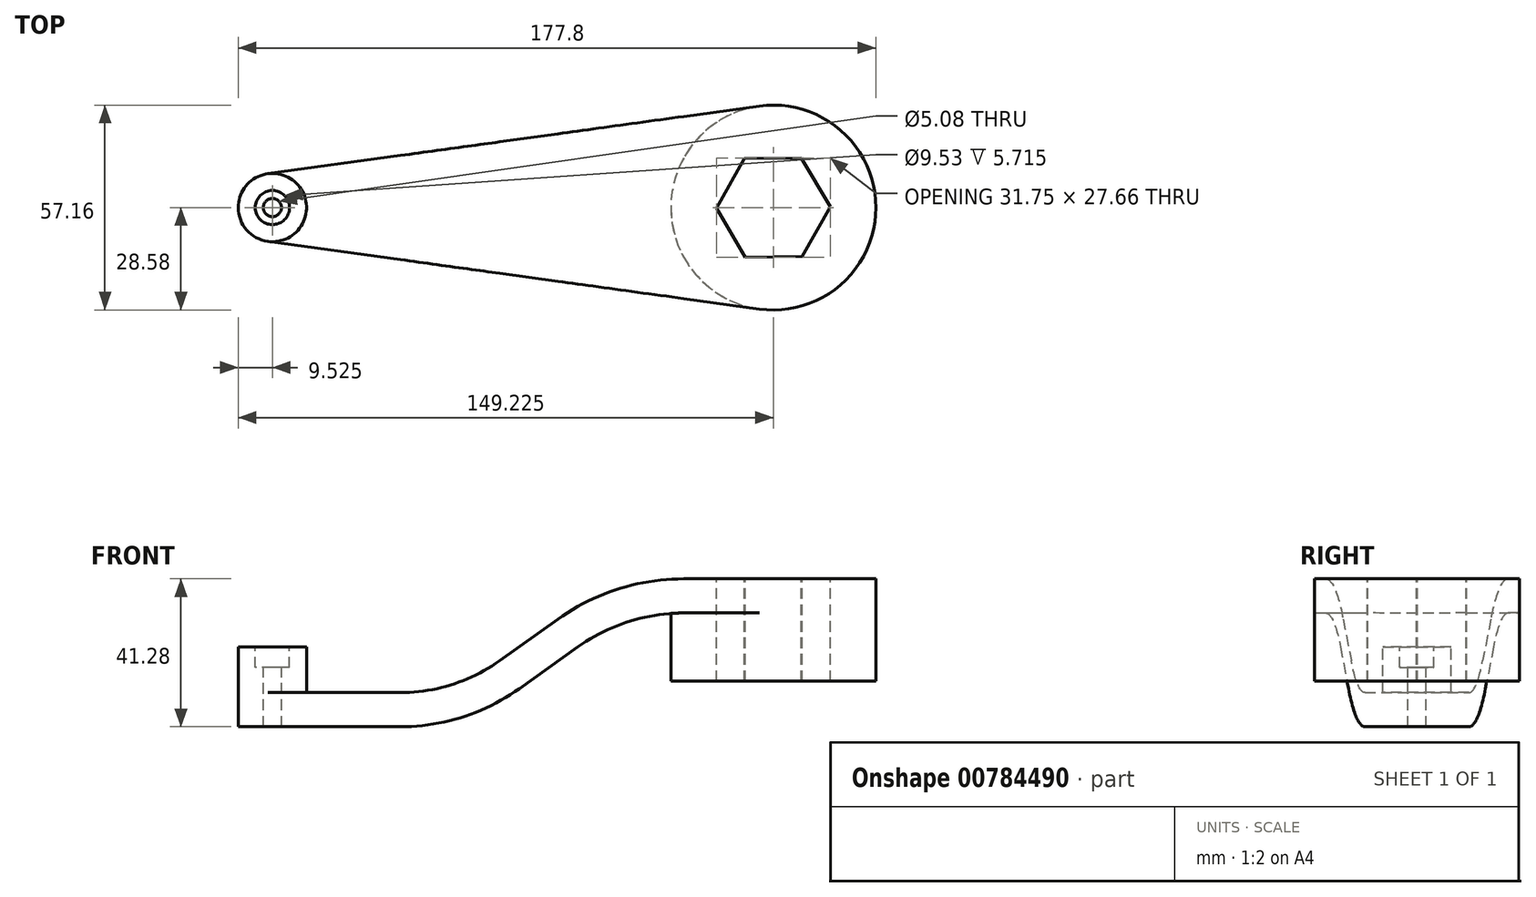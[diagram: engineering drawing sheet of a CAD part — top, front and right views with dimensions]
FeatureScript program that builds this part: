
annotation { "Feature Type Name" : "Feature", "Feature Type Description" : "" }
export const myFeature = defineFeature(function(context is Context, id is Id, definition is map)
    precondition{}
    {
        {
            var Q0;
            Q0=qCreatedBy(makeId("Front.planeOp"),FACE);
            var sketch = newSketch(context, id + "F0", { "sketchPlane" : qUnion([Q0])});
            skLineSegment(sketch, "E0", {"start": v(0, 0) * mm, "end": v(0, -9.53) * mm});
            skLineSegment(sketch, "E1", {"start": v(0, -9.53) * mm, "end": v(-53.57, -9.53) * mm});
            skPoint(sketch, "E2", {"position": v(-69.85, -9.53) * mm});
            skPoint(sketch, "E3", {"position": v(-114.3, -41.28) * mm});
            skLineSegment(sketch, "E4", {"start": v(-83.1, -18.99) * mm, "end": v(-99.4, -30.63) * mm});
            skLineSegment(sketch, "E5", {"start": v(-132.61, -41.28) * mm, "end": v(-177.8, -41.28) * mm});
            skArc(sketch, "E6.filletArc", {"start": v(-53.57, -9.52) * mm, "mid": v(-69.07, -11.95) * mm, "end": v(-83.1, -18.99) * mm});
            skArc(sketch, "E7.filletArc", {"start": v(-132.61, -41.28) * mm, "mid": v(-115.17, -38.55) * mm, "end": v(-99.4, -30.63) * mm});
            skLineSegment(sketch, "E8.0", {"start": v(-132.61, -31.75) * mm, "end": v(-177.8, -31.75) * mm});
            skArc(sketch, "E9.0", {"start": v(-132.61, -31.75) * mm, "mid": v(-118.08, -29.48) * mm, "end": v(-104.93, -22.88) * mm});
            skLineSegment(sketch, "E10.0", {"start": v(-88.63, -11.24) * mm, "end": v(-104.93, -22.88) * mm});
            skArc(sketch, "E11.0", {"start": v(-53.57, 0) * mm, "mid": v(-71.98, -2.88) * mm, "end": v(-88.63, -11.24) * mm});
            skLineSegment(sketch, "E12.0", {"start": v(0, 0) * mm, "end": v(-53.57, 0) * mm});
            skLineSegment(sketch, "E13", {"start": v(-177.8, -31.75) * mm, "end": v(-177.8, -41.28) * mm});
            skSolve(sketch);
        }
        {
            var Q0;
            Q0 = qSketchRegion(id + "F0", true);
            extrude(context, id + "F1", {"entities" : qUnion([Q0]), "endBound" : BoundingType.SYMMETRIC, "depth" : 57.15 * mm, "offsetDistance" : 25.4 * mm});
        }
        {
            var Q0;
            Q0=makeQuery(id+"F1.opExtrude","SWEPT_FACE",FACE,{"disambiguationData":[OSD([sQuery(id+"F0.wireOp",EDGE,"E12.0")])]});
            var sketch = newSketch(context, id + "F2", { "sketchPlane" : qUnion([Q0])});
            skLineSegment(sketch, "E14", {"start": v(0, 0) * mm, "end": v(-190.14, 0) * mm, "construction": true});
            skArc(sketch, "E15", {"start": v(-32.47, -28.3) * mm, "mid": v(0, 0) * mm, "end": v(-32.47, 28.3) * mm});
            skArc(sketch, "E16", {"start": v(-169.57, 9.44) * mm, "mid": v(-177.8, 0) * mm, "end": v(-169.57, -9.44) * mm});
            skLineSegment(sketch, "E17", {"start": v(-169.57, 9.44) * mm, "end": v(-32.47, 28.3) * mm});
            skLineSegment(sketch, "E18.MirrorCS", {"start": v(-169.57, -9.44) * mm, "end": v(-32.47, -28.3) * mm});
            skSolve(sketch);
        }
        {
            var Q0;
            Q0 = qSketchRegion(id + "F2", true);
            extrude(context, id + "F3", {"entities" : qUnion([Q0]), "operationType" : NewBodyOperationType.INTERSECT, "endBound" : BoundingType.THROUGH_ALL, "oppositeDirection" : true, "depth" : 25.4 * mm, "offsetDistance" : 25.4 * mm});
        }
        {
            var Q0;
            Q0=makeQuery(id+"F1.opExtrude","SWEPT_FACE",FACE,{"disambiguationData":[OSD([sQuery(id+"F0.wireOp",EDGE,"E8.0")])]});
            var sketch = newSketch(context, id + "F4", { "sketchPlane" : qUnion([Q0])});
            skCircle(sketch, "E19", {"center": v(-168.28, 0) * mm, "radius": 9.53 * mm});
            skSolve(sketch);
        }
        {
            var Q0;
            Q0 = qSketchRegion(id + "F4", true);
            extrude(context, id + "F5", {"entities" : qUnion([Q0]), "operationType" : NewBodyOperationType.ADD, "depth" : 12.7 * mm, "offsetDistance" : 25.4 * mm});
        }
        {
            var Q0;
            Q0=makeQuery(id+"F1.opExtrude","SWEPT_FACE",FACE,{"disambiguationData":[OSD([sQuery(id+"F0.wireOp",EDGE,"E1")])]});
            var sketch = newSketch(context, id + "F6", { "sketchPlane" : qUnion([Q0])});
            skCircle(sketch, "E20", {"center": v(-28.57, 0) * mm, "radius": 28.58 * mm});
            skSolve(sketch);
        }
        {
            var Q0;
            Q0 = qSketchRegion(id + "F6", true);
            extrude(context, id + "F7", {"entities" : qUnion([Q0]), "operationType" : NewBodyOperationType.ADD, "depth" : 19.05 * mm, "offsetDistance" : 25.4 * mm});
        }
        {
            var Q0;
            Q0=makeQuery(id+"F1.opExtrude","SWEPT_FACE",FACE,{"disambiguationData":[OSD([sQuery(id+"F0.wireOp",EDGE,"E12.0")])]});
            var sketch = newSketch(context, id + "F8", { "sketchPlane" : qUnion([Q0])});
            skCircle(sketch, "E21", {"center": v(-28.58, 0) * mm, "radius": 15.88 * mm});
            skCircle(sketch, "E22.cCircle", {"center": v(-28.58, 0) * mm, "radius": 15.88 * mm, "construction": true});
            skLineSegment(sketch, "E22.0", {"start": v(-36.66, 13.66) * mm, "end": v(-20.78, 13.83) * mm});
            skLineSegment(sketch, "E22.1", {"start": v(-20.78, 13.83) * mm, "end": v(-12.7, 0.17) * mm});
            skLineSegment(sketch, "E22.2", {"start": v(-12.7, 0.17) * mm, "end": v(-20.5, -13.66) * mm});
            skLineSegment(sketch, "E22.3", {"start": v(-20.5, -13.66) * mm, "end": v(-36.37, -13.83) * mm});
            skLineSegment(sketch, "E22.4", {"start": v(-36.37, -13.83) * mm, "end": v(-44.45, -0.17) * mm});
            skLineSegment(sketch, "E22.5", {"start": v(-44.45, -0.17) * mm, "end": v(-36.66, 13.66) * mm});
            skSolve(sketch);
        }
        {
            var Q0;
            Q0=makeQuery(id+"F8.imprint","IMPRINT",FACE,{"disambiguationData":[TD([[makeQuery(id+"F8.imprint","IMPRINT",EDGE,{"derivedFrom":sQuery(id+"F8.wireOp",EDGE,"E22.0")}),-1.0]])]});
            extrude(context, id + "F9", {"entities" : qUnion([Q0]), "operationType" : NewBodyOperationType.REMOVE, "endBound" : BoundingType.THROUGH_ALL, "oppositeDirection" : true, "depth" : 25.4 * mm, "offsetDistance" : 25.4 * mm});
        }
        {
            var Q0;
            Q0=makeQuery(id+"F5.opExtrude","CAP_FACE",FACE,{"disambiguationData":[OSD([sQuery(id+"F4.wireOp",EDGE,"E19")])],"isStart":false});
            var sketch = newSketch(context, id + "F10", { "sketchPlane" : qUnion([Q0])});
            skCircle(sketch, "E23", {"center": v(-168.28, 0) * mm, "radius": 9.53 * mm});
            skSolve(sketch);
        }
        {
            var Q0;
            Q0=sQuery(id+"F10.wireOp",VERTEX,"E23.center");
            var Q1;
            Q1=makeQuery(id+"F1.opExtrude","SWEPT_BODY",BODY,{"disambiguationData":[OSD([sQuery(id+"F0.wireOp",EDGE,"E0"),sQuery(id+"F0.wireOp",EDGE,"E1"),sQuery(id+"F0.wireOp",EDGE,"E4"),sQuery(id+"F0.wireOp",EDGE,"E5"),sQuery(id+"F0.wireOp",EDGE,"E6.filletArc"),sQuery(id+"F0.wireOp",EDGE,"E7.filletArc"),sQuery(id+"F0.wireOp",EDGE,"E8.0"),sQuery(id+"F0.wireOp",EDGE,"E9.0"),sQuery(id+"F0.wireOp",EDGE,"E10.0"),sQuery(id+"F0.wireOp",EDGE,"E11.0"),sQuery(id+"F0.wireOp",EDGE,"E12.0"),sQuery(id+"F0.wireOp",EDGE,"E13")])]});
            hole(context, id + "F11", {"style" : HoleStyle.C_BORE, "endStyle" : HoleEndStyle.BLIND, "holeDiameter" : 5.08 * mm, "cBoreDiameter" : 9.52 * mm, "cBoreDepth" : 5.7 * mm, "majorDiameter" : 6.35 * mm, "holeDepth" : 76.2 * mm, "isTappedThrough" : true, "tappedDepth" : 12.7 * mm, "tapClearance" : 3, "startFromSketch" : true, "locations" : qUnion([Q0]), "scope" : qUnion([Q1])});
        }
    });
